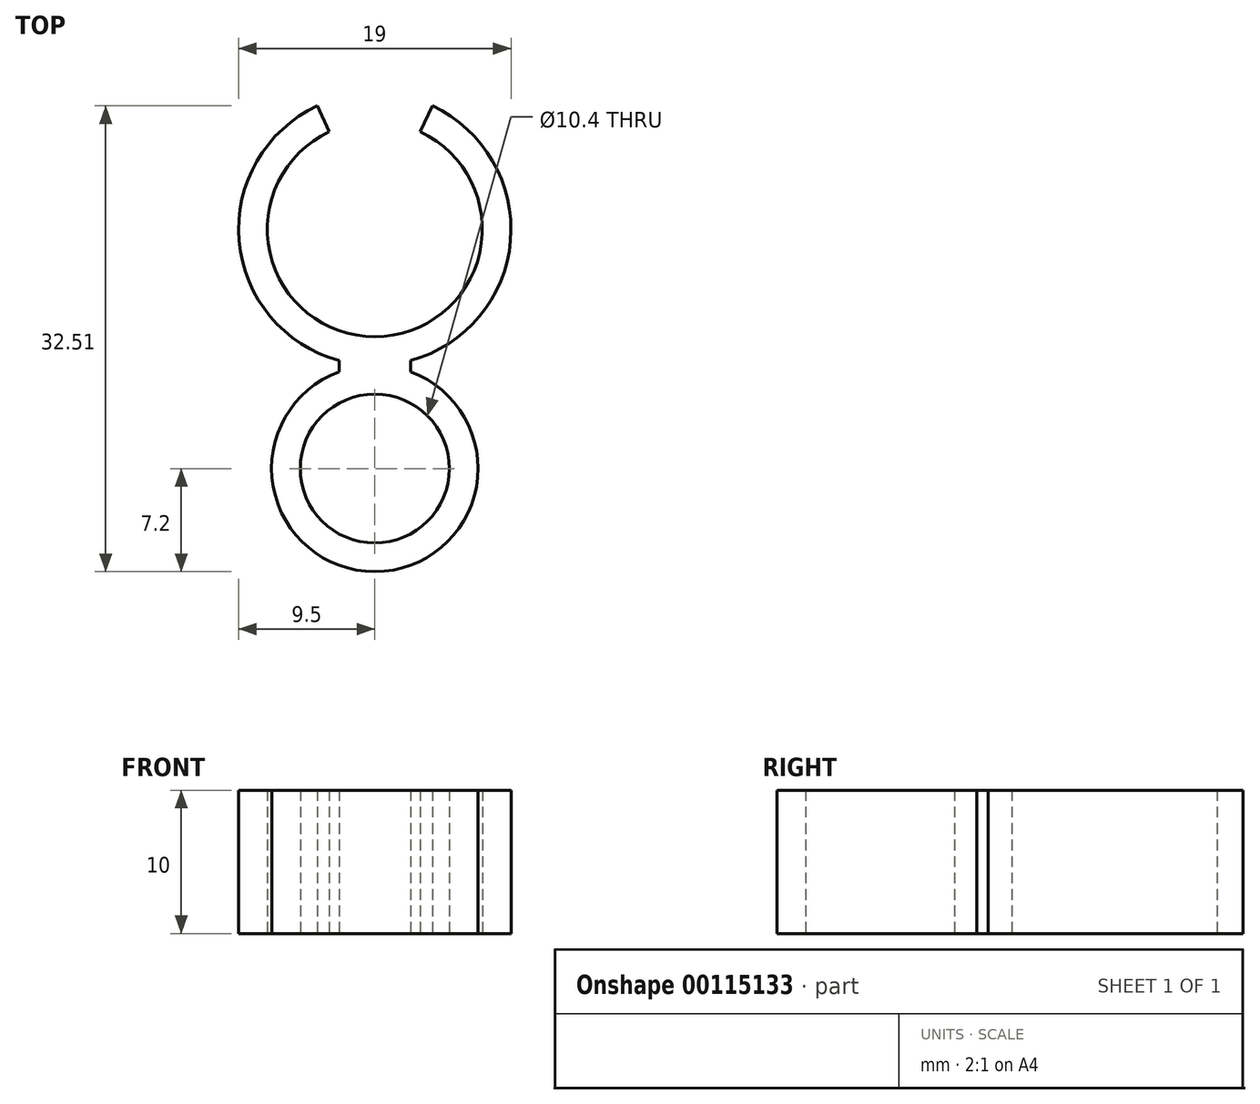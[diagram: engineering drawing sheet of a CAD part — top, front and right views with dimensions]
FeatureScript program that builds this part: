
annotation { "Feature Type Name" : "Feature", "Feature Type Description" : "" }
export const myFeature = defineFeature(function(context is Context, id is Id, definition is map)
    precondition{}
    {
        {
            var Q0;
            Q0=qCreatedBy(makeId("Top.planeOp"),FACE);
            var sketch = newSketch(context, id + "F0", { "sketchPlane" : qUnion([Q0])});
            skCircle(sketch, "E0", {"center": v(0, 0) * mm, "radius": 5.2 * mm});
            skCircle(sketch, "E1.0", {"center": v(0, 0) * mm, "radius": 7.2 * mm});
            skCircle(sketch, "E2", {"center": v(0, 16.7) * mm, "radius": 7.5 * mm});
            skCircle(sketch, "E3.0", {"center": v(0, 16.7) * mm, "radius": 9.5 * mm});
            skLineSegment(sketch, "E4", {"start": v(-2.5, 9.63) * mm, "end": v(-2.5, 4.56) * mm});
            skLineSegment(sketch, "E5", {"start": v(0, 16.7) * mm, "end": v(0, 0) * mm, "construction": true});
            skLineSegment(sketch, "E6.MirrorCS", {"start": v(2.5, 9.63) * mm, "end": v(2.5, 4.56) * mm});
            skLineSegment(sketch, "E7", {"start": v(0, 16.7) * mm, "end": v(-4.01, 25.3) * mm});
            skLineSegment(sketch, "E8.MirrorCS", {"start": v(0, 16.7) * mm, "end": v(4.01, 25.3) * mm});
            skSolve(sketch);
        }
        {
            var Q0;
            {var subQ0=sQuery(id+"F0.wireOp",EDGE,"E4");var subQ1=sQuery(id+"F0.wireOp",EDGE,"E0");var subQ2=makeQuery(id+"F0.imprint","INTERSECT",VERTEX,{"derivedFrom":[subQ1,subQ0]});Q0=makeQuery(id+"F0.imprint","IMPRINT",FACE,{"disambiguationData":[TD([[makeQuery(id+"F0.imprint","IMPRINT",EDGE,{"disambiguationData":[TD([[subQ2,-1.0]])],"derivedFrom":subQ1}),-1.0]])]});}
            var Q1;
            {var subQ0=sQuery(id+"F0.wireOp",EDGE,"E6.MirrorCS");var subQ1=sQuery(id+"F0.wireOp",EDGE,"E1.0");var subQ2=makeQuery(id+"F0.imprint","INTERSECT",VERTEX,{"derivedFrom":[subQ1,subQ0]});Q1=makeQuery(id+"F0.imprint","IMPRINT",FACE,{"disambiguationData":[TD([[makeQuery(id+"F0.imprint","IMPRINT",EDGE,{"disambiguationData":[TD([[subQ2,-1.0]])],"derivedFrom":subQ1}),-1.0]])]});}
            var Q2;
            {var subQ0=sQuery(id+"F0.wireOp",EDGE,"E4");var subQ1=sQuery(id+"F0.wireOp",EDGE,"E1.0");var subQ2=makeQuery(id+"F0.imprint","INTERSECT",VERTEX,{"derivedFrom":[subQ1,subQ0]});Q2=makeQuery(id+"F0.imprint","IMPRINT",FACE,{"disambiguationData":[TD([[makeQuery(id+"F0.imprint","IMPRINT",EDGE,{"disambiguationData":[TD([[subQ2,1.0]])],"derivedFrom":subQ1}),-1.0]])]});}
            var Q3;
            {var subQ0=sQuery(id+"F0.wireOp",EDGE,"E6.MirrorCS");var subQ1=sQuery(id+"F0.wireOp",EDGE,"E2");var subQ2=makeQuery(id+"F0.imprint","INTERSECT",VERTEX,{"derivedFrom":[subQ1,subQ0]});Q3=makeQuery(id+"F0.imprint","IMPRINT",FACE,{"disambiguationData":[TD([[makeQuery(id+"F0.imprint","IMPRINT",EDGE,{"disambiguationData":[TD([[subQ2,-1.0]])],"derivedFrom":subQ1}),-1.0]])]});}
            var Q4;
            {var subQ0=sQuery(id+"F0.wireOp",EDGE,"E4");var subQ1=sQuery(id+"F0.wireOp",EDGE,"E0");var subQ2=makeQuery(id+"F0.imprint","INTERSECT",VERTEX,{"derivedFrom":[subQ1,subQ0]});Q4=makeQuery(id+"F0.imprint","IMPRINT",FACE,{"disambiguationData":[TD([[makeQuery(id+"F0.imprint","IMPRINT",EDGE,{"disambiguationData":[TD([[subQ2,1.0]])],"derivedFrom":subQ1}),-1.0]])]});}
            var Q5;
            {var subQ0=sQuery(id+"F0.wireOp",EDGE,"E4");var subQ1=sQuery(id+"F0.wireOp",EDGE,"E2");var subQ2=makeQuery(id+"F0.imprint","INTERSECT",VERTEX,{"derivedFrom":[subQ1,subQ0]});Q5=makeQuery(id+"F0.imprint","IMPRINT",FACE,{"disambiguationData":[TD([[makeQuery(id+"F0.imprint","IMPRINT",EDGE,{"disambiguationData":[TD([[subQ2,-1.0]])],"derivedFrom":subQ1}),-1.0]])]});}
            var Q6;
            {var subQ0=sQuery(id+"F0.wireOp",EDGE,"E4");var subQ1=sQuery(id+"F0.wireOp",EDGE,"E2");var subQ2=makeQuery(id+"F0.imprint","INTERSECT",VERTEX,{"derivedFrom":[subQ1,subQ0]});Q6=makeQuery(id+"F0.imprint","IMPRINT",FACE,{"disambiguationData":[TD([[makeQuery(id+"F0.imprint","IMPRINT",EDGE,{"disambiguationData":[TD([[subQ2,1.0]])],"derivedFrom":subQ1}),-1.0]])]});}
            extrude(context, id + "F1", {"entities" : qUnion([Q0, Q1, Q2, Q3, Q4, Q5, Q6]), "depth" : 10 * mm});
        }
    });
